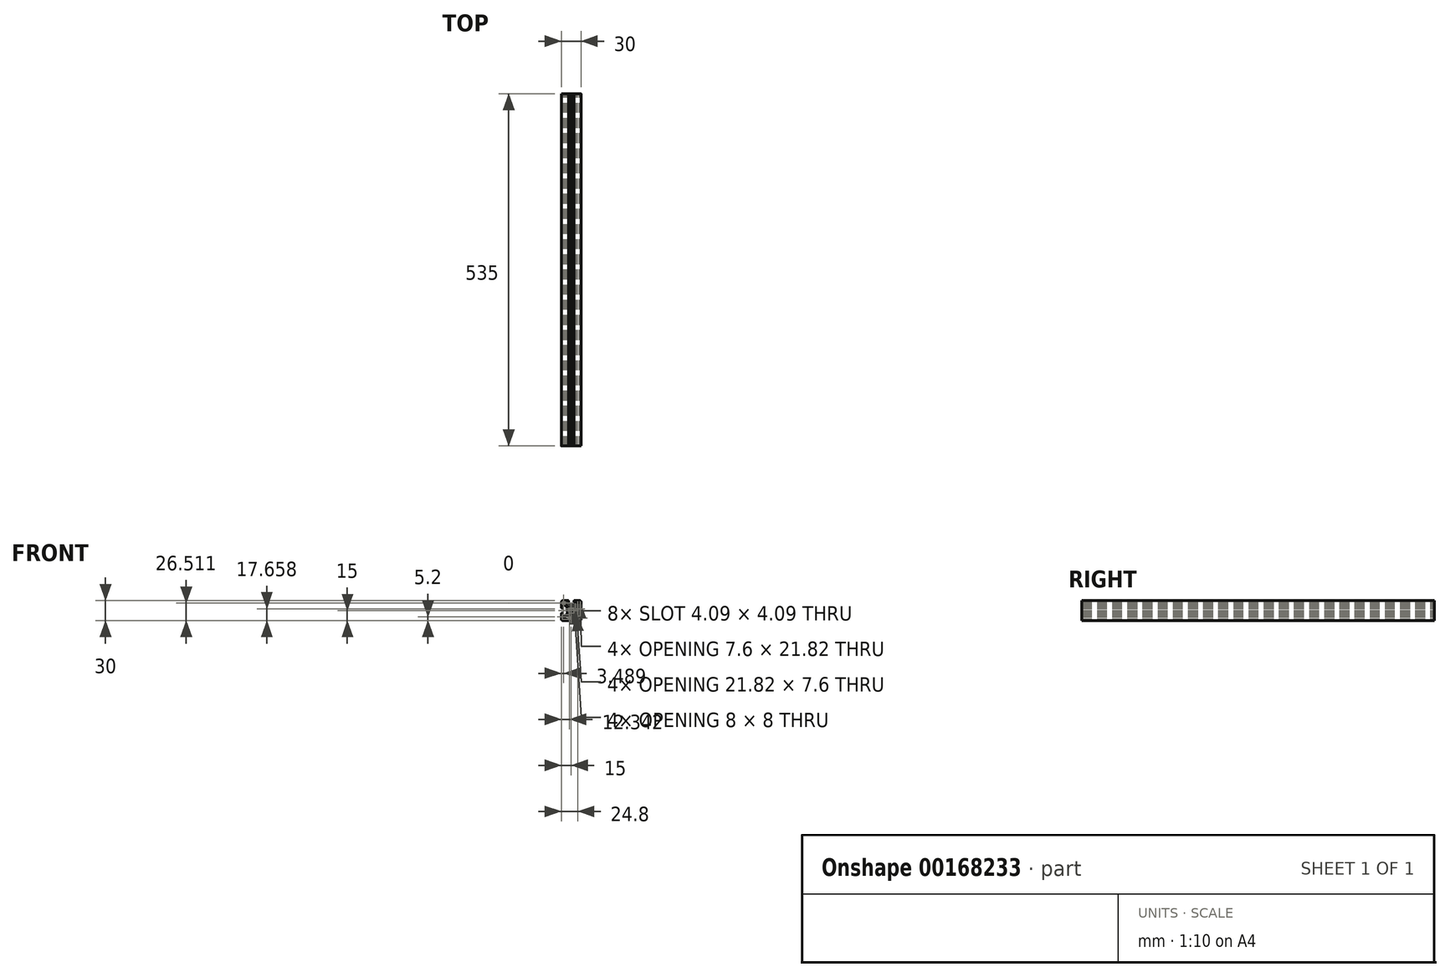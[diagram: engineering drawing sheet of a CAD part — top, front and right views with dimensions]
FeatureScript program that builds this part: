
annotation { "Feature Type Name" : "Feature", "Feature Type Description" : "" }
export const myFeature = defineFeature(function(context is Context, id is Id, definition is map)
    precondition{}
    {
        {
            var Q0;
            Q0=qCreatedBy(makeId("Front.planeOp"),FACE);
            var sketch = newSketch(context, id + "F0", { "sketchPlane" : qUnion([Q0])});
            skLineSegment(sketch, "E0", {"start": v(0, 17) * mm, "end": v(0, -17) * mm});
            skLineSegment(sketch, "E1", {"start": v(-17, 0) * mm, "end": v(17, 0) * mm});
            skLineSegment(sketch, "E2", {"start": v(-13, 15) * mm, "end": v(-4.3, 15) * mm});
            skLineSegment(sketch, "E3", {"start": v(-13, -15) * mm, "end": v(13, -15) * mm});
            skLineSegment(sketch, "E4", {"start": v(15, 13) * mm, "end": v(15, -13) * mm});
            skLineSegment(sketch, "E5", {"start": v(-15, 13) * mm, "end": v(-15, 4.3) * mm});
            skArc(sketch, "E6", {"start": v(15, 13) * mm, "mid": v(14.41, 14.41) * mm, "end": v(13, 15) * mm});
            skArc(sketch, "E7", {"start": v(-13, 15) * mm, "mid": v(-14.41, 14.41) * mm, "end": v(-15, 13) * mm});
            skArc(sketch, "E8", {"start": v(-15, -13) * mm, "mid": v(-14.41, -14.41) * mm, "end": v(-13, -15) * mm});
            skArc(sketch, "E9", {"start": v(13, -15) * mm, "mid": v(14.41, -14.41) * mm, "end": v(15, -13) * mm});
            skLineSegment(sketch, "E10", {"start": v(-13, -8.25) * mm, "end": v(-13, -4.3) * mm});
            skLineSegment(sketch, "E11", {"start": v(13, 8.19) * mm, "end": v(13, -7.25) * mm});
            skLineSegment(sketch, "E12", {"start": v(-8.19, -13) * mm, "end": v(7.25, -13) * mm});
            skLineSegment(sketch, "E13", {"start": v(-14.7, -4) * mm, "end": v(-13.3, -4) * mm});
            skLineSegment(sketch, "E14", {"start": v(-14.7, 4) * mm, "end": v(-13.3, 4) * mm});
            skLineSegment(sketch, "E15", {"start": v(-13, 4.3) * mm, "end": v(-13, 8.25) * mm});
            skLineSegment(sketch, "E16", {"start": v(4.3, 15) * mm, "end": v(13, 15) * mm});
            skLineSegment(sketch, "E17", {"start": v(-9.66, -8.25) * mm, "end": v(-13, -8.25) * mm});
            skLineSegment(sketch, "E18", {"start": v(-9.66, 8.25) * mm, "end": v(-13, 8.25) * mm});
            skLineSegment(sketch, "E19", {"start": v(4.59, 6) * mm, "end": v(0.65, 6) * mm});
            skLineSegment(sketch, "E20", {"start": v(4.17, -6) * mm, "end": v(-4.17, -6) * mm});
            skLineSegment(sketch, "E21", {"start": v(6, -4.17) * mm, "end": v(6, 4.17) * mm});
            skLineSegment(sketch, "E22", {"start": v(-6, -4.59) * mm, "end": v(-6, -2.5) * mm});
            skLineSegment(sketch, "E23", {"start": v(-4.59, 6) * mm, "end": v(-8.25, 9.66) * mm});
            skLineSegment(sketch, "E24", {"start": v(-6, 4.59) * mm, "end": v(-9.66, 8.25) * mm});
            skLineSegment(sketch, "E25", {"start": v(6.3, 4.88) * mm, "end": v(9.16, 7.74) * mm});
            skLineSegment(sketch, "E26", {"start": v(4.59, 6) * mm, "end": v(8.25, 9.66) * mm});
            skLineSegment(sketch, "E27", {"start": v(6.3, -4.88) * mm, "end": v(9.37, -7.96) * mm});
            skLineSegment(sketch, "E28", {"start": v(4.88, -6.3) * mm, "end": v(7.96, -9.37) * mm});
            skLineSegment(sketch, "E29", {"start": v(-4.88, -6.3) * mm, "end": v(-7.74, -9.16) * mm});
            skLineSegment(sketch, "E30", {"start": v(-6, -4.59) * mm, "end": v(-9.66, -8.25) * mm});
            skLineSegment(sketch, "E31", {"start": v(-15, -4.3) * mm, "end": v(-15, -13) * mm});
            skLineSegment(sketch, "E32", {"start": v(-4, 14.7) * mm, "end": v(-4, 13.3) * mm});
            skLineSegment(sketch, "E33", {"start": v(4, 14.7) * mm, "end": v(4, 13.3) * mm});
            skLineSegment(sketch, "E34", {"start": v(8.25, 9.66) * mm, "end": v(8.25, 13) * mm});
            skLineSegment(sketch, "E35", {"start": v(-8.25, 9.66) * mm, "end": v(-8.25, 13) * mm});
            skLineSegment(sketch, "E36", {"start": v(-4.3, 13) * mm, "end": v(-8.25, 13) * mm});
            skLineSegment(sketch, "E37", {"start": v(4.3, 13) * mm, "end": v(8.25, 13) * mm});
            skLineSegment(sketch, "E38", {"start": v(9.45, 8.45) * mm, "end": v(9.45, 11.07) * mm});
            skLineSegment(sketch, "E39", {"start": v(9.45, 11.07) * mm, "end": v(9.91, 12.35) * mm});
            skArc(sketch, "E40", {"start": v(12.78, 10.14) * mm, "mid": v(12.86, 13.2) * mm, "end": v(9.91, 12.35) * mm});
            skArc(sketch, "E41", {"start": v(12.78, 10.14) * mm, "mid": v(12.35, 9.27) * mm, "end": v(12.85, 8.45) * mm});
            skArc(sketch, "E42", {"start": v(13, 8.19) * mm, "mid": v(12.96, 8.34) * mm, "end": v(12.85, 8.45) * mm});
            skArc(sketch, "E43", {"start": v(-9.91, 12.35) * mm, "mid": v(-13.04, 13.04) * mm, "end": v(-12.35, 9.91) * mm});
            skLineSegment(sketch, "E44", {"start": v(-9.55, 11.34) * mm, "end": v(-9.91, 12.35) * mm});
            skLineSegment(sketch, "E45", {"start": v(-11.34, 9.55) * mm, "end": v(-12.35, 9.91) * mm});
            skArc(sketch, "E46", {"start": v(-11.34, 9.55) * mm, "mid": v(-9.87, 9.87) * mm, "end": v(-9.55, 11.34) * mm});
            skArc(sketch, "E47", {"start": v(9.91, -12.35) * mm, "mid": v(13.04, -13.04) * mm, "end": v(12.35, -9.91) * mm});
            skLineSegment(sketch, "E48", {"start": v(11.34, -9.55) * mm, "end": v(12.35, -9.91) * mm});
            skLineSegment(sketch, "E49", {"start": v(9.55, -11.34) * mm, "end": v(9.91, -12.35) * mm});
            skArc(sketch, "E50", {"start": v(11.34, -9.55) * mm, "mid": v(9.87, -9.87) * mm, "end": v(9.55, -11.34) * mm});
            skArc(sketch, "E51", {"start": v(6.3, 4.88) * mm, "mid": v(6.08, 4.55) * mm, "end": v(6, 4.17) * mm});
            skArc(sketch, "E52", {"start": v(6, -4.17) * mm, "mid": v(6.08, -4.55) * mm, "end": v(6.3, -4.88) * mm});
            skLineSegment(sketch, "E53", {"start": v(10.08, -8.25) * mm, "end": v(12, -8.25) * mm});
            skArc(sketch, "E54", {"start": v(9.37, -7.96) * mm, "mid": v(9.7, -8.17) * mm, "end": v(10.08, -8.25) * mm});
            skArc(sketch, "E55", {"start": v(12, -8.25) * mm, "mid": v(12.7, -7.96) * mm, "end": v(13, -7.25) * mm});
            skArc(sketch, "E56", {"start": v(9.16, 7.74) * mm, "mid": v(9.37, 8.07) * mm, "end": v(9.45, 8.45) * mm});
            skLineSegment(sketch, "E57", {"start": v(8.25, -10.08) * mm, "end": v(8.25, -12) * mm});
            skLineSegment(sketch, "E58", {"start": v(-8.45, -9.45) * mm, "end": v(-11.07, -9.45) * mm});
            skLineSegment(sketch, "E59", {"start": v(-11.07, -9.45) * mm, "end": v(-12.35, -9.91) * mm});
            skArc(sketch, "E60", {"start": v(-12.35, -9.91) * mm, "mid": v(-13.2, -12.86) * mm, "end": v(-10.14, -12.78) * mm});
            skArc(sketch, "E61", {"start": v(-8.45, -12.85) * mm, "mid": v(-9.27, -12.35) * mm, "end": v(-10.14, -12.78) * mm});
            skArc(sketch, "E62", {"start": v(-8.45, -12.85) * mm, "mid": v(-8.34, -12.96) * mm, "end": v(-8.19, -13) * mm});
            skArc(sketch, "E63", {"start": v(-8.45, -9.45) * mm, "mid": v(-8.07, -9.37) * mm, "end": v(-7.74, -9.16) * mm});
            skArc(sketch, "E64", {"start": v(-4.17, -6) * mm, "mid": v(-4.55, -6.08) * mm, "end": v(-4.88, -6.3) * mm});
            skArc(sketch, "E65", {"start": v(4.88, -6.3) * mm, "mid": v(4.55, -6.08) * mm, "end": v(4.17, -6) * mm});
            skArc(sketch, "E66", {"start": v(8.25, -10.08) * mm, "mid": v(8.17, -9.7) * mm, "end": v(7.96, -9.37) * mm});
            skArc(sketch, "E67", {"start": v(7.25, -13) * mm, "mid": v(7.96, -12.7) * mm, "end": v(8.25, -12) * mm});
            skLineSegment(sketch, "E68", {"start": v(3.5, 4) * mm, "end": v(2, 4) * mm});
            skLineSegment(sketch, "E69", {"start": v(4, -3.5) * mm, "end": v(4, -2) * mm});
            skLineSegment(sketch, "E70", {"start": v(3.5, -4) * mm, "end": v(2, -4) * mm});
            skLineSegment(sketch, "E71", {"start": v(-4, -3.5) * mm, "end": v(-4, -2) * mm});
            skLineSegment(sketch, "E72", {"start": v(-2.5, 6) * mm, "end": v(-1.22, 5.75) * mm});
            skLineSegment(sketch, "E73", {"start": v(0, 5.7) * mm, "end": v(-0.4, 5.93) * mm});
            skLineSegment(sketch, "E74", {"start": v(0, 5.7) * mm, "end": v(0.4, 5.93) * mm});
            skLineSegment(sketch, "E75", {"start": v(-2.5, 6) * mm, "end": v(-4.59, 6) * mm});
            skArc(sketch, "E76", {"start": v(0.65, 6) * mm, "mid": v(0.52, 5.98) * mm, "end": v(0.4, 5.93) * mm});
            skArc(sketch, "E77", {"start": v(-0.4, 5.93) * mm, "mid": v(-0.65, 6) * mm, "end": v(-0.9, 5.93) * mm});
            skLineSegment(sketch, "E78", {"start": v(-1.22, 5.75) * mm, "end": v(-0.9, 5.93) * mm});
            skArc(sketch, "E79", {"start": v(-6, 0.65) * mm, "mid": v(-5.98, 0.52) * mm, "end": v(-5.93, 0.4) * mm});
            skLineSegment(sketch, "E80", {"start": v(-6, -2.5) * mm, "end": v(-5.75, -1.22) * mm});
            skLineSegment(sketch, "E81", {"start": v(-5.7, 0) * mm, "end": v(-5.93, -0.4) * mm});
            skLineSegment(sketch, "E82", {"start": v(-5.7, 0) * mm, "end": v(-5.93, 0.4) * mm});
            skArc(sketch, "E83", {"start": v(-5.93, -0.4) * mm, "mid": v(-6, -0.65) * mm, "end": v(-5.93, -0.9) * mm});
            skLineSegment(sketch, "E84", {"start": v(-5.75, -1.22) * mm, "end": v(-5.93, -0.9) * mm});
            skLineSegment(sketch, "E85", {"start": v(-6, 0.65) * mm, "end": v(-6, 4.59) * mm});
            skArc(sketch, "E86", {"start": v(4, 13.3) * mm, "mid": v(4.09, 13.09) * mm, "end": v(4.3, 13) * mm});
            skArc(sketch, "E87", {"start": v(4.3, 15) * mm, "mid": v(4.09, 14.91) * mm, "end": v(4, 14.7) * mm});
            skArc(sketch, "E88", {"start": v(-4.3, 13) * mm, "mid": v(-4.09, 13.09) * mm, "end": v(-4, 13.3) * mm});
            skArc(sketch, "E89", {"start": v(-4, 14.7) * mm, "mid": v(-4.09, 14.91) * mm, "end": v(-4.3, 15) * mm});
            skArc(sketch, "E90", {"start": v(-13.3, 4) * mm, "mid": v(-13.09, 4.09) * mm, "end": v(-13, 4.3) * mm});
            skArc(sketch, "E91", {"start": v(-15, 4.3) * mm, "mid": v(-14.91, 4.09) * mm, "end": v(-14.7, 4) * mm});
            skArc(sketch, "E92", {"start": v(-13, -4.3) * mm, "mid": v(-13.09, -4.09) * mm, "end": v(-13.3, -4) * mm});
            skArc(sketch, "E93", {"start": v(-14.7, -4) * mm, "mid": v(-14.91, -4.09) * mm, "end": v(-15, -4.3) * mm});
            skArc(sketch, "E94", {"start": v(0.99, 3.25) * mm, "mid": v(0, 3.4) * mm, "end": v(-0.99, 3.25) * mm});
            skArc(sketch, "E95", {"start": v(-1.5, 3.58) * mm, "mid": v(-1.32, 3.3) * mm, "end": v(-0.99, 3.25) * mm});
            skArc(sketch, "E96", {"start": v(-1.5, 3.58) * mm, "mid": v(-1.67, 3.88) * mm, "end": v(-2, 4) * mm});
            skArc(sketch, "E97", {"start": v(0.99, 3.25) * mm, "mid": v(1.32, 3.3) * mm, "end": v(1.5, 3.58) * mm});
            skArc(sketch, "E98", {"start": v(2, 4) * mm, "mid": v(1.67, 3.88) * mm, "end": v(1.5, 3.58) * mm});
            skLineSegment(sketch, "E99", {"start": v(-2, 4) * mm, "end": v(-3.5, 4) * mm});
            skArc(sketch, "E100", {"start": v(-3.5, 4) * mm, "mid": v(-3.85, 3.85) * mm, "end": v(-4, 3.5) * mm});
            skArc(sketch, "E101", {"start": v(4, 3.5) * mm, "mid": v(3.85, 3.85) * mm, "end": v(3.5, 4) * mm});
            skArc(sketch, "E102", {"start": v(3.5, -4) * mm, "mid": v(3.85, -3.85) * mm, "end": v(4, -3.5) * mm});
            skArc(sketch, "E103", {"start": v(-4, -3.5) * mm, "mid": v(-3.85, -3.85) * mm, "end": v(-3.5, -4) * mm});
            skArc(sketch, "E104", {"start": v(-3.25, 0.99) * mm, "mid": v(-3.4, 0) * mm, "end": v(-3.25, -0.99) * mm});
            skArc(sketch, "E105", {"start": v(-3.58, -1.5) * mm, "mid": v(-3.3, -1.32) * mm, "end": v(-3.25, -0.99) * mm});
            skArc(sketch, "E106", {"start": v(-3.58, -1.5) * mm, "mid": v(-3.88, -1.67) * mm, "end": v(-4, -2) * mm});
            skArc(sketch, "E107", {"start": v(-3.25, 0.99) * mm, "mid": v(-3.3, 1.32) * mm, "end": v(-3.58, 1.5) * mm});
            skArc(sketch, "E108", {"start": v(-4, 2) * mm, "mid": v(-3.88, 1.67) * mm, "end": v(-3.58, 1.5) * mm});
            skArc(sketch, "E109", {"start": v(3.25, -0.99) * mm, "mid": v(3.4, 0) * mm, "end": v(3.25, 0.99) * mm});
            skArc(sketch, "E110", {"start": v(3.58, 1.5) * mm, "mid": v(3.3, 1.32) * mm, "end": v(3.25, 0.99) * mm});
            skArc(sketch, "E111", {"start": v(3.58, 1.5) * mm, "mid": v(3.88, 1.67) * mm, "end": v(4, 2) * mm});
            skArc(sketch, "E112", {"start": v(3.25, -0.99) * mm, "mid": v(3.3, -1.32) * mm, "end": v(3.58, -1.5) * mm});
            skArc(sketch, "E113", {"start": v(4, -2) * mm, "mid": v(3.88, -1.67) * mm, "end": v(3.58, -1.5) * mm});
            skArc(sketch, "E114", {"start": v(-0.99, -3.25) * mm, "mid": v(0, -3.4) * mm, "end": v(0.99, -3.25) * mm});
            skArc(sketch, "E115", {"start": v(-0.99, -3.25) * mm, "mid": v(-1.32, -3.3) * mm, "end": v(-1.5, -3.58) * mm});
            skArc(sketch, "E116", {"start": v(-2, -4) * mm, "mid": v(-1.67, -3.88) * mm, "end": v(-1.5, -3.58) * mm});
            skArc(sketch, "E117", {"start": v(1.5, -3.58) * mm, "mid": v(1.32, -3.3) * mm, "end": v(0.99, -3.25) * mm});
            skArc(sketch, "E118", {"start": v(1.5, -3.58) * mm, "mid": v(1.67, -3.88) * mm, "end": v(2, -4) * mm});
            skLineSegment(sketch, "E119", {"start": v(4, 2) * mm, "end": v(4, 3.5) * mm});
            skLineSegment(sketch, "E120", {"start": v(-2, -4) * mm, "end": v(-3.5, -4) * mm});
            skLineSegment(sketch, "E121", {"start": v(-4, 2) * mm, "end": v(-4, 3.5) * mm});
            skCircle(sketch, "E122", {"center": v(0, 0) * mm, "radius": 3.4 * mm});
            skLineSegment(sketch, "E123", {"start": v(11.7, 15.6) * mm, "end": v(11.7, 7.8) * mm});
            skLineSegment(sketch, "E124", {"start": v(7.8, 11.7) * mm, "end": v(15.6, 11.7) * mm});
            skLineSegment(sketch, "E125", {"start": v(11.7, -7.8) * mm, "end": v(11.7, -15.6) * mm});
            skLineSegment(sketch, "E126", {"start": v(7.8, -11.7) * mm, "end": v(15.6, -11.7) * mm});
            skLineSegment(sketch, "E127", {"start": v(-11.7, -7.8) * mm, "end": v(-11.7, -15.6) * mm});
            skLineSegment(sketch, "E128", {"start": v(-15.6, -11.7) * mm, "end": v(-7.8, -11.7) * mm});
            skLineSegment(sketch, "E129", {"start": v(-11.7, 15.6) * mm, "end": v(-11.7, 7.8) * mm});
            skLineSegment(sketch, "E130", {"start": v(-15.6, 11.7) * mm, "end": v(-7.8, 11.7) * mm});
            skSolve(sketch);
        }
        {
            var Q0;
            Q0=qCreatedBy(makeId("Front.planeOp"),FACE);
            var sketch = newSketch(context, id + "F1", { "sketchPlane" : qUnion([Q0])});
            skArc(sketch, "E131.0", {"start": v(-8.45, -12.85) * mm, "mid": v(-9.27, -12.35) * mm, "end": v(-10.14, -12.78) * mm});
            skLineSegment(sketch, "E131.1", {"start": v(-4.88, -6.3) * mm, "end": v(-7.74, -9.16) * mm});
            skLineSegment(sketch, "E131.3", {"start": v(4.17, -6) * mm, "end": v(-4.17, -6) * mm});
            skLineSegment(sketch, "E131.4", {"start": v(-4.3, 13) * mm, "end": v(-8.25, 13) * mm});
            skArc(sketch, "E131.5", {"start": v(-11.34, 9.55) * mm, "mid": v(-9.87, 9.87) * mm, "end": v(-9.55, 11.34) * mm});
            skLineSegment(sketch, "E131.6", {"start": v(-6, -4.59) * mm, "end": v(-9.66, -8.25) * mm});
            skLineSegment(sketch, "E131.7", {"start": v(6, -4.17) * mm, "end": v(6, 4.17) * mm});
            skLineSegment(sketch, "E131.8", {"start": v(-6, 0.65) * mm, "end": v(-6, 4.59) * mm});
            skLineSegment(sketch, "E131.9", {"start": v(4.3, 13) * mm, "end": v(8.25, 13) * mm});
            skLineSegment(sketch, "E131.10", {"start": v(-6, -4.59) * mm, "end": v(-6, -2.5) * mm});
            skLineSegment(sketch, "E131.11", {"start": v(9.45, 8.45) * mm, "end": v(9.45, 11.07) * mm});
            skLineSegment(sketch, "E131.12", {"start": v(-4.59, 6) * mm, "end": v(-8.25, 9.66) * mm});
            skLineSegment(sketch, "E131.13", {"start": v(-8.25, 9.66) * mm, "end": v(-8.25, 13) * mm});
            skLineSegment(sketch, "E131.15", {"start": v(8.25, 9.66) * mm, "end": v(8.25, 13) * mm});
            skArc(sketch, "E131.16", {"start": v(11.34, -9.55) * mm, "mid": v(9.87, -9.87) * mm, "end": v(9.55, -11.34) * mm});
            skLineSegment(sketch, "E131.17", {"start": v(-9.66, 8.25) * mm, "end": v(-13, 8.25) * mm});
            skLineSegment(sketch, "E131.18", {"start": v(4.59, 6) * mm, "end": v(0.65, 6) * mm});
            skLineSegment(sketch, "E131.19", {"start": v(-8.19, -13) * mm, "end": v(7.25, -13) * mm});
            skLineSegment(sketch, "E131.20", {"start": v(13, 8.19) * mm, "end": v(13, -7.25) * mm});
            skLineSegment(sketch, "E131.21", {"start": v(-13, -8.25) * mm, "end": v(-13, -4.3) * mm});
            skArc(sketch, "E131.23", {"start": v(13, -15) * mm, "mid": v(14.41, -14.41) * mm, "end": v(15, -13) * mm});
            skArc(sketch, "E131.24", {"start": v(-15, -13) * mm, "mid": v(-14.41, -14.41) * mm, "end": v(-13, -15) * mm});
            skArc(sketch, "E131.25", {"start": v(-13, 15) * mm, "mid": v(-14.41, 14.41) * mm, "end": v(-15, 13) * mm});
            skArc(sketch, "E131.26", {"start": v(15, 13) * mm, "mid": v(14.41, 14.41) * mm, "end": v(13, 15) * mm});
            skLineSegment(sketch, "E131.27", {"start": v(-15, 13) * mm, "end": v(-15, 4.3) * mm});
            skLineSegment(sketch, "E131.28", {"start": v(15, 13) * mm, "end": v(15, -13) * mm});
            skLineSegment(sketch, "E131.29", {"start": v(-9.66, -8.25) * mm, "end": v(-13, -8.25) * mm});
            skLineSegment(sketch, "E131.30", {"start": v(-13, -15) * mm, "end": v(13, -15) * mm});
            skLineSegment(sketch, "E131.31", {"start": v(-13, 15) * mm, "end": v(-4.3, 15) * mm});
            skLineSegment(sketch, "E131.32", {"start": v(-13, 4.3) * mm, "end": v(-13, 8.25) * mm});
            skLineSegment(sketch, "E131.33", {"start": v(4.88, -6.3) * mm, "end": v(7.96, -9.37) * mm});
            skArc(sketch, "E131.34", {"start": v(-12.35, -9.91) * mm, "mid": v(-13.2, -12.86) * mm, "end": v(-10.14, -12.78) * mm});
            skLineSegment(sketch, "E131.35", {"start": v(-2.5, 6) * mm, "end": v(-4.59, 6) * mm});
            skLineSegment(sketch, "E131.37", {"start": v(6.3, -4.88) * mm, "end": v(9.37, -7.96) * mm});
            skArc(sketch, "E131.38", {"start": v(-9.91, 12.35) * mm, "mid": v(-13.04, 13.04) * mm, "end": v(-12.35, 9.91) * mm});
            skLineSegment(sketch, "E131.39", {"start": v(4.3, 15) * mm, "end": v(13, 15) * mm});
            skLineSegment(sketch, "E131.41", {"start": v(4.59, 6) * mm, "end": v(8.25, 9.66) * mm});
            skLineSegment(sketch, "E131.42", {"start": v(-8.45, -9.45) * mm, "end": v(-11.07, -9.45) * mm});
            skLineSegment(sketch, "E131.43", {"start": v(6.3, 4.88) * mm, "end": v(9.16, 7.74) * mm});
            skLineSegment(sketch, "E131.46", {"start": v(-15, -4.3) * mm, "end": v(-15, -13) * mm});
            skArc(sketch, "E131.47", {"start": v(9.91, -12.35) * mm, "mid": v(13.04, -13.04) * mm, "end": v(12.35, -9.91) * mm});
            skLineSegment(sketch, "E131.48", {"start": v(-6, 4.59) * mm, "end": v(-9.66, 8.25) * mm});
            skArc(sketch, "E131.49", {"start": v(12.78, 10.14) * mm, "mid": v(12.86, 13.2) * mm, "end": v(9.91, 12.35) * mm});
            skArc(sketch, "E131.50", {"start": v(3.25, -0.99) * mm, "mid": v(3.4, 0) * mm, "end": v(3.25, 0.99) * mm});
            skArc(sketch, "E131.51", {"start": v(0.99, 3.25) * mm, "mid": v(0, 3.4) * mm, "end": v(-0.99, 3.25) * mm});
            skArc(sketch, "E131.52", {"start": v(-0.99, -3.25) * mm, "mid": v(0, -3.4) * mm, "end": v(0.99, -3.25) * mm});
            skLineSegment(sketch, "E131.53", {"start": v(8.25, -10.08) * mm, "end": v(8.25, -12) * mm});
            skArc(sketch, "E131.54", {"start": v(-3.25, 0.99) * mm, "mid": v(-3.4, 0) * mm, "end": v(-3.25, -0.99) * mm});
            skArc(sketch, "E131.55", {"start": v(-0.99, -3.25) * mm, "mid": v(-1.32, -3.3) * mm, "end": v(-1.5, -3.58) * mm});
            skLineSegment(sketch, "E131.56", {"start": v(-11.34, 9.55) * mm, "end": v(-12.35, 9.91) * mm});
            skLineSegment(sketch, "E131.57", {"start": v(-2, 4) * mm, "end": v(-3.5, 4) * mm});
            skLineSegment(sketch, "E131.58", {"start": v(3.5, 4) * mm, "end": v(2, 4) * mm});
            skArc(sketch, "E131.59", {"start": v(6, -4.17) * mm, "mid": v(6.08, -4.55) * mm, "end": v(6.3, -4.88) * mm});
            skArc(sketch, "E131.60", {"start": v(-2, -4) * mm, "mid": v(-1.67, -3.88) * mm, "end": v(-1.5, -3.58) * mm});
            skArc(sketch, "E131.61", {"start": v(-3.5, 4) * mm, "mid": v(-3.85, 3.85) * mm, "end": v(-4, 3.5) * mm});
            skArc(sketch, "E131.62", {"start": v(3.58, 1.5) * mm, "mid": v(3.3, 1.32) * mm, "end": v(3.25, 0.99) * mm});
            skLineSegment(sketch, "E131.63", {"start": v(4, -3.5) * mm, "end": v(4, -2) * mm});
            skLineSegment(sketch, "E131.64", {"start": v(10.08, -8.25) * mm, "end": v(12, -8.25) * mm});
            skArc(sketch, "E131.65", {"start": v(1.5, -3.58) * mm, "mid": v(1.32, -3.3) * mm, "end": v(0.99, -3.25) * mm});
            skArc(sketch, "E131.66", {"start": v(4, 3.5) * mm, "mid": v(3.85, 3.85) * mm, "end": v(3.5, 4) * mm});
            skArc(sketch, "E131.67", {"start": v(4, 13.3) * mm, "mid": v(4.09, 13.09) * mm, "end": v(4.3, 13) * mm});
            skLineSegment(sketch, "E131.68", {"start": v(3.5, -4) * mm, "end": v(2, -4) * mm});
            skArc(sketch, "E131.69", {"start": v(9.37, -7.96) * mm, "mid": v(9.7, -8.17) * mm, "end": v(10.08, -8.25) * mm});
            skArc(sketch, "E131.70", {"start": v(1.5, -3.58) * mm, "mid": v(1.67, -3.88) * mm, "end": v(2, -4) * mm});
            skArc(sketch, "E131.71", {"start": v(3.5, -4) * mm, "mid": v(3.85, -3.85) * mm, "end": v(4, -3.5) * mm});
            skArc(sketch, "E131.72", {"start": v(12, -8.25) * mm, "mid": v(12.7, -7.96) * mm, "end": v(13, -7.25) * mm});
            skLineSegment(sketch, "E131.73", {"start": v(9.45, 11.07) * mm, "end": v(9.91, 12.35) * mm});
            skLineSegment(sketch, "E131.74", {"start": v(4, 2) * mm, "end": v(4, 3.5) * mm});
            skArc(sketch, "E131.75", {"start": v(-4, -3.5) * mm, "mid": v(-3.85, -3.85) * mm, "end": v(-3.5, -4) * mm});
            skArc(sketch, "E131.76", {"start": v(4.3, 15) * mm, "mid": v(4.09, 14.91) * mm, "end": v(4, 14.7) * mm});
            skLineSegment(sketch, "E131.77", {"start": v(-4, -3.5) * mm, "end": v(-4, -2) * mm});
            skArc(sketch, "E131.78", {"start": v(8.25, -10.08) * mm, "mid": v(8.17, -9.7) * mm, "end": v(7.96, -9.37) * mm});
            skArc(sketch, "E131.79", {"start": v(-8.45, -9.45) * mm, "mid": v(-8.07, -9.37) * mm, "end": v(-7.74, -9.16) * mm});
            skArc(sketch, "E131.80", {"start": v(6.3, 4.88) * mm, "mid": v(6.08, 4.55) * mm, "end": v(6, 4.17) * mm});
            skArc(sketch, "E131.81", {"start": v(7.25, -13) * mm, "mid": v(7.96, -12.7) * mm, "end": v(8.25, -12) * mm});
            skLineSegment(sketch, "E131.82", {"start": v(4, 14.7) * mm, "end": v(4, 13.3) * mm});
            skLineSegment(sketch, "E131.83", {"start": v(9.55, -11.34) * mm, "end": v(9.91, -12.35) * mm});
            skArc(sketch, "E131.84", {"start": v(4.88, -6.3) * mm, "mid": v(4.55, -6.08) * mm, "end": v(4.17, -6) * mm});
            skArc(sketch, "E131.85", {"start": v(0.65, 6) * mm, "mid": v(0.52, 5.98) * mm, "end": v(0.4, 5.93) * mm});
            skArc(sketch, "E131.86", {"start": v(-4, 2) * mm, "mid": v(-3.88, 1.67) * mm, "end": v(-3.58, 1.5) * mm});
            skLineSegment(sketch, "E131.87", {"start": v(-9.55, 11.34) * mm, "end": v(-9.91, 12.35) * mm});
            skArc(sketch, "E131.88", {"start": v(-3.25, 0.99) * mm, "mid": v(-3.3, 1.32) * mm, "end": v(-3.58, 1.5) * mm});
            skLineSegment(sketch, "E131.89", {"start": v(-11.07, -9.45) * mm, "end": v(-12.35, -9.91) * mm});
            skLineSegment(sketch, "E131.90", {"start": v(11.34, -9.55) * mm, "end": v(12.35, -9.91) * mm});
            skArc(sketch, "E131.91", {"start": v(-4.17, -6) * mm, "mid": v(-4.55, -6.08) * mm, "end": v(-4.88, -6.3) * mm});
            skLineSegment(sketch, "E131.92", {"start": v(-6, -2.5) * mm, "end": v(-5.75, -1.22) * mm});
            skArc(sketch, "E131.93", {"start": v(13, 8.19) * mm, "mid": v(12.96, 8.34) * mm, "end": v(12.85, 8.45) * mm});
            skLineSegment(sketch, "E131.94", {"start": v(-4, 2) * mm, "end": v(-4, 3.5) * mm});
            skArc(sketch, "E131.95", {"start": v(12.78, 10.14) * mm, "mid": v(12.35, 9.27) * mm, "end": v(12.85, 8.45) * mm});
            skArc(sketch, "E131.96", {"start": v(3.58, 1.5) * mm, "mid": v(3.88, 1.67) * mm, "end": v(4, 2) * mm});
            skLineSegment(sketch, "E131.97", {"start": v(-2.5, 6) * mm, "end": v(-1.22, 5.75) * mm});
            skLineSegment(sketch, "E131.98", {"start": v(-2, -4) * mm, "end": v(-3.5, -4) * mm});
            skArc(sketch, "E131.99", {"start": v(9.16, 7.74) * mm, "mid": v(9.37, 8.07) * mm, "end": v(9.45, 8.45) * mm});
            skArc(sketch, "E131.100", {"start": v(-0.4, 5.93) * mm, "mid": v(-0.65, 6) * mm, "end": v(-0.9, 5.93) * mm});
            skLineSegment(sketch, "E131.101", {"start": v(-5.75, -1.22) * mm, "end": v(-5.93, -0.9) * mm});
            skLineSegment(sketch, "E131.102", {"start": v(-1.22, 5.75) * mm, "end": v(-0.9, 5.93) * mm});
            skArc(sketch, "E131.103", {"start": v(-8.45, -12.85) * mm, "mid": v(-8.34, -12.96) * mm, "end": v(-8.19, -13) * mm});
            skArc(sketch, "E131.104", {"start": v(2, 4) * mm, "mid": v(1.67, 3.88) * mm, "end": v(1.5, 3.58) * mm});
            skArc(sketch, "E131.105", {"start": v(0.99, 3.25) * mm, "mid": v(1.32, 3.3) * mm, "end": v(1.5, 3.58) * mm});
            skArc(sketch, "E131.106", {"start": v(4, -2) * mm, "mid": v(3.88, -1.67) * mm, "end": v(3.58, -1.5) * mm});
            skLineSegment(sketch, "E131.107", {"start": v(-14.7, 4) * mm, "end": v(-13.3, 4) * mm});
            skArc(sketch, "E131.108", {"start": v(-15, 4.3) * mm, "mid": v(-14.91, 4.09) * mm, "end": v(-14.7, 4) * mm});
            skLineSegment(sketch, "E131.109", {"start": v(0, 5.7) * mm, "end": v(0.4, 5.93) * mm});
            skArc(sketch, "E131.110", {"start": v(-13.3, 4) * mm, "mid": v(-13.09, 4.09) * mm, "end": v(-13, 4.3) * mm});
            skArc(sketch, "E131.111", {"start": v(-3.58, -1.5) * mm, "mid": v(-3.88, -1.67) * mm, "end": v(-4, -2) * mm});
            skArc(sketch, "E131.112", {"start": v(-1.5, 3.58) * mm, "mid": v(-1.67, 3.88) * mm, "end": v(-2, 4) * mm});
            skLineSegment(sketch, "E131.113", {"start": v(0, 5.7) * mm, "end": v(-0.4, 5.93) * mm});
            skArc(sketch, "E131.114", {"start": v(-3.58, -1.5) * mm, "mid": v(-3.3, -1.32) * mm, "end": v(-3.25, -0.99) * mm});
            skArc(sketch, "E131.115", {"start": v(3.25, -0.99) * mm, "mid": v(3.3, -1.32) * mm, "end": v(3.58, -1.5) * mm});
            skArc(sketch, "E131.116", {"start": v(-1.5, 3.58) * mm, "mid": v(-1.32, 3.3) * mm, "end": v(-0.99, 3.25) * mm});
            skLineSegment(sketch, "E131.117", {"start": v(-5.7, 0) * mm, "end": v(-5.93, 0.4) * mm});
            skArc(sketch, "E131.118", {"start": v(-5.93, -0.4) * mm, "mid": v(-6, -0.65) * mm, "end": v(-5.93, -0.9) * mm});
            skLineSegment(sketch, "E131.119", {"start": v(-4, 14.7) * mm, "end": v(-4, 13.3) * mm});
            skArc(sketch, "E131.120", {"start": v(-4, 14.7) * mm, "mid": v(-4.09, 14.91) * mm, "end": v(-4.3, 15) * mm});
            skArc(sketch, "E131.121", {"start": v(-4.3, 13) * mm, "mid": v(-4.09, 13.09) * mm, "end": v(-4, 13.3) * mm});
            skArc(sketch, "E131.122", {"start": v(-14.7, -4) * mm, "mid": v(-14.91, -4.09) * mm, "end": v(-15, -4.3) * mm});
            skArc(sketch, "E131.123", {"start": v(-6, 0.65) * mm, "mid": v(-5.98, 0.52) * mm, "end": v(-5.93, 0.4) * mm});
            skLineSegment(sketch, "E131.124", {"start": v(-5.7, 0) * mm, "end": v(-5.93, -0.4) * mm});
            skLineSegment(sketch, "E131.125", {"start": v(-14.7, -4) * mm, "end": v(-13.3, -4) * mm});
            skArc(sketch, "E131.126", {"start": v(-13, -4.3) * mm, "mid": v(-13.09, -4.09) * mm, "end": v(-13.3, -4) * mm});
            skSolve(sketch);
        }
        {
            var Q0;
            Q0=makeQuery(id+"F1.imprint","IMPRINT",FACE,{"disambiguationData":[TD([[makeQuery(id+"F1.imprint","IMPRINT",EDGE,{"derivedFrom":sQuery(id+"F1.wireOp",EDGE,"E131.0")}),1.0]])]});
            extrude(context, id + "F2", {"entities" : qUnion([Q0]), "endBound" : BoundingType.SYMMETRIC, "depth" : 535 * mm});
        }
    });
